# Revit family: НЕВАТОМ_Клапан KPNZ-60(90)-D-F2-04(12)-MN, Версия 2
name_source: partatom
category: Арматура воздуховодов
revit_build: Autodesk Revit 2017 (Build: 20170118_1100(x64)
units: mm (PartAtom-declared; Revit-internal decimal feet)

## family parameters
Всегда вертикально = Нет
На основе рабочей плоскости = Нет
Общий = Нет
При загрузке вырезать с полостями = Нет
Размер круглого соединителя = Использовать диаметр
Тип детали = Вставляется

## types (1)
- KPNZ-60(90)-D-F2-04(12)-MN220(24)
    ADSK_Единица измерения = шт.
    ADSK_Завод-изготовитель = НЕВАТОМ
    ADSK_Количество = 1
    ADSK_Материал наименование = Оцинкованная сталь
    ADSK_Полная мощность = 0 В·А
    ADSK_Потеря давления воздуха = 0.0 Па
    ADSK_Расход воздуха = 0.0 л/с
    ADSK_Ток = 0 А
    H = 140 мм
    L = 320 мм
    Nevatom_URL = https://t.me
    P = 200 мм
    a = 0 мм
    d = 9 мм
    t = 1 мм
    Высота привода = 100 мм
    Длина площадки = 150 мм
    Закрыто = Нет
    Материал корпуса = Материал корпуса
    Открыто = Да
    Ширина площадки = 98 мм
    Ширина привода = 100 мм
